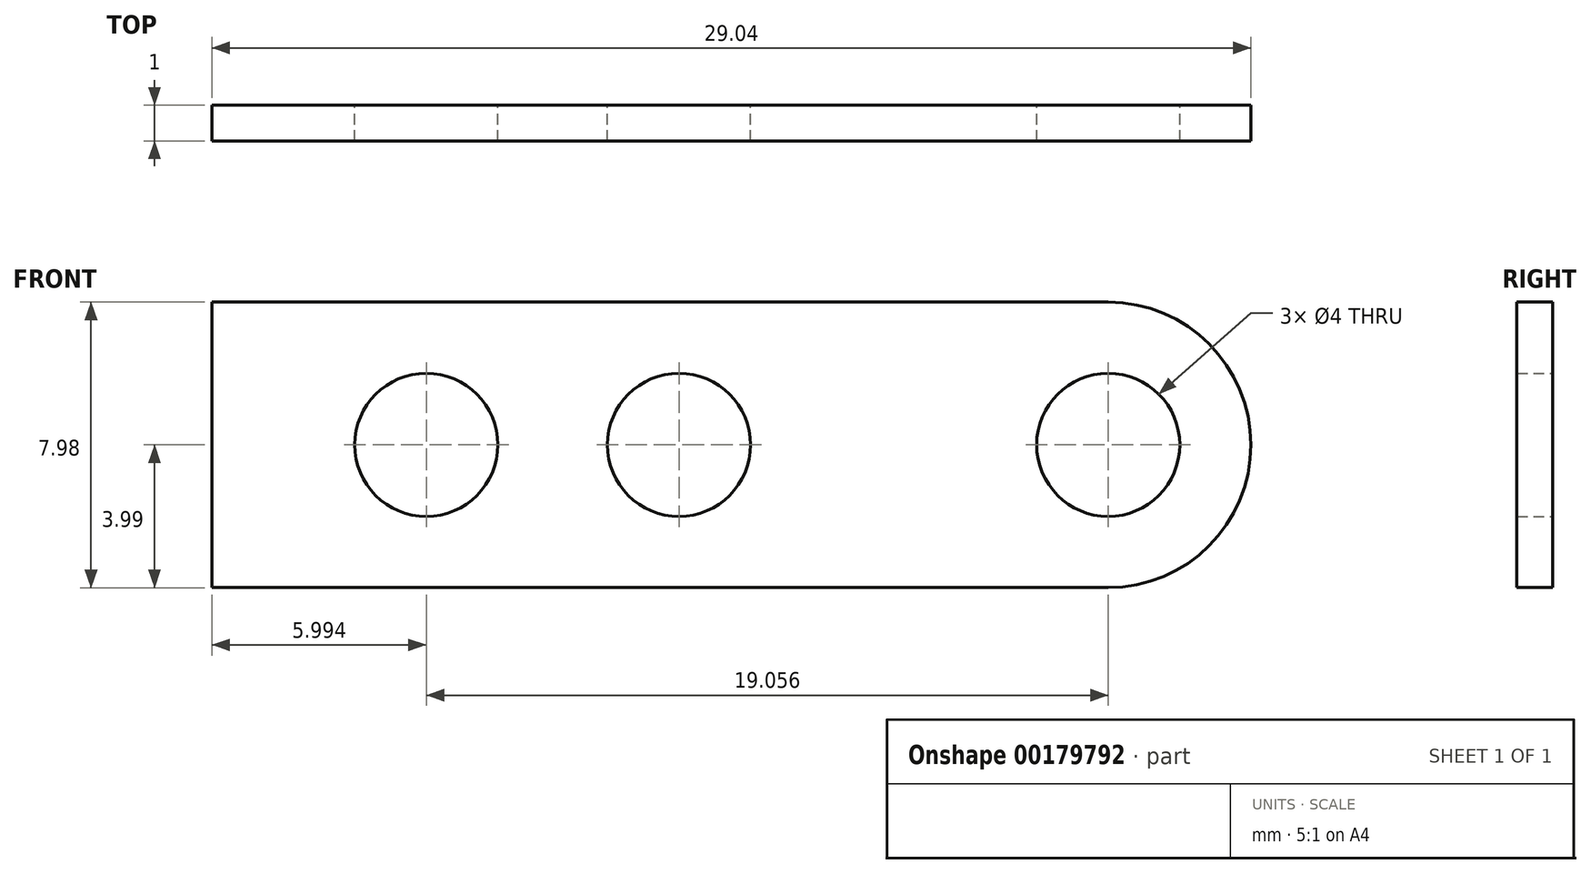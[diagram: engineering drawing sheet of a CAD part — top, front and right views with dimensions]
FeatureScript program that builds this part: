
annotation { "Feature Type Name" : "Feature", "Feature Type Description" : "" }
export const myFeature = defineFeature(function(context is Context, id is Id, definition is map)
    precondition{}
    {
        {
            var Q0;
            Q0=qCreatedBy(makeId("Front.planeOp"),FACE);
            var sketch = newSketch(context, id + "F0", { "sketchPlane" : qUnion([Q0])});
            skCircle(sketch, "E0", {"center": v(0, 0) * mm, "radius": 2 * mm});
            skArc(sketch, "E1", {"start": v(0, -3.99) * mm, "mid": v(3.99, 0) * mm, "end": v(0, 3.99) * mm});
            skLineSegment(sketch, "E2", {"start": v(0, 3.99) * mm, "end": v(-25.05, 3.99) * mm});
            skLineSegment(sketch, "E3", {"start": v(-25.05, 3.99) * mm, "end": v(-25.05, -3.99) * mm});
            skLineSegment(sketch, "E4", {"start": v(-25.05, -3.99) * mm, "end": v(0, -3.99) * mm});
            skCircle(sketch, "E5", {"center": v(-19.06, 0) * mm, "radius": 2 * mm});
            skCircle(sketch, "E6", {"center": v(-12, 0) * mm, "radius": 2 * mm});
            skLineSegment(sketch, "E7", {"start": v(-6, 3.99) * mm, "end": v(-6, -3.99) * mm, "construction": true});
            skLineSegment(sketch, "E8", {"start": v(-4, 3.99) * mm, "end": v(-4, -3.99) * mm, "construction": true});
            skSolve(sketch);
        }
        {
            var Q0;
            Q0 = qSketchRegion(id + "F0", true);
            extrude(context, id + "F1", {"entities" : qUnion([Q0]), "endBound" : BoundingType.SYMMETRIC, "depth" : 1 * mm});
        }
    });
